# Revit family: Gira_086100
name_source: partatom
category: Electrical Fixtures
revit_build: Autodesk Revit 2017 (Build: 20160225_1515(x64)
units: mm (PartAtom-declared; Revit-internal decimal feet)

## family parameters
Cut with Voids When Loaded = No
Host = Face
Maintain Annotation Orientation = No
Part Type = Normal
Room Calculation Point = No
Round Connector Dimension = Use Diameter
Shared = No

## types (1)
- Cut-off relay 2-g DRA Blind
    BIM = https://media.live.bim.site 00_REG 2.5.rfa
    BIMSITE_PRODUCT_ID = 5451681ee89bcbe04bd01c97bd85773aa633bdb1
    Cost = 0 $
    Default Elevation = 1219 mm
    Description = Cut-off relay 2g DRA Blind 2-gang cut-off relay,DRA Features: - Simultaneous control of more than one blind drive. - In each case, two drives are electrically decoupled with one cut-off relay. - With two auxiliary inputs for the individual operation of the blinds and a central input for a central function, e.g. of a timer or for implementing central controllers for distribution among several RCCBs.,Notes : - The DRA cut-off relay is mounted on a cap profile rail.
    GTIN = 4010337861003
    HAN = 086100
    HeinzeBIM = https://www.heinze.de
    Manufacturer = Gira
    URL = https://www.gira.de

## geometry (parser evidence)
native form markers: Blend x4, Sweep x3
no freeform markers — native parametric forms only
